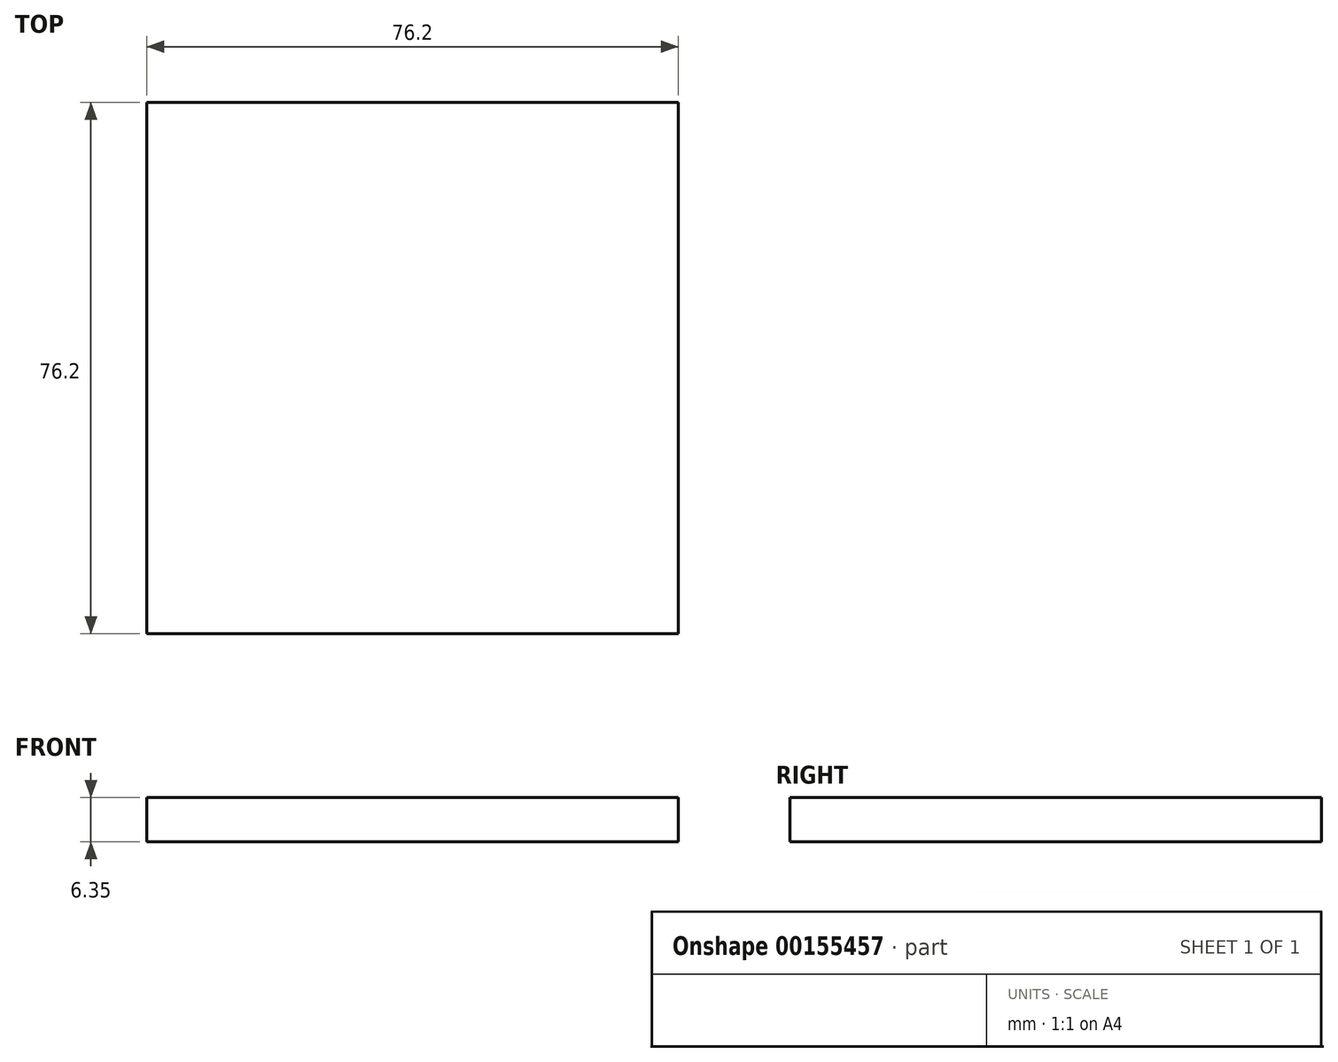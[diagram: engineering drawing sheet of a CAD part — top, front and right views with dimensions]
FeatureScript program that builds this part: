
annotation { "Feature Type Name" : "Feature", "Feature Type Description" : "" }
export const myFeature = defineFeature(function(context is Context, id is Id, definition is map)
    precondition{}
    {
        {
            var Q0;
            Q0=qCreatedBy(makeId("Top.planeOp"),FACE);
            var sketch = newSketch(context, id + "F0", { "sketchPlane" : qUnion([Q0])});
            skLineSegment(sketch, "E0.bottom", {"start": v(0, 0) * mm, "end": v(76.2, 0) * mm});
            skLineSegment(sketch, "E0.top", {"start": v(0, 76.2) * mm, "end": v(76.2, 76.2) * mm});
            skLineSegment(sketch, "E0.left", {"start": v(0, 0) * mm, "end": v(0, 76.2) * mm});
            skLineSegment(sketch, "E0.right", {"start": v(76.2, 0) * mm, "end": v(76.2, 76.2) * mm});
            skSolve(sketch);
        }
        {
            var Q0;
            Q0 = qSketchRegion(id + "F0", true);
            extrude(context, id + "F1", {"entities" : qUnion([Q0]), "depth" : 6.35 * mm});
        }
    });
